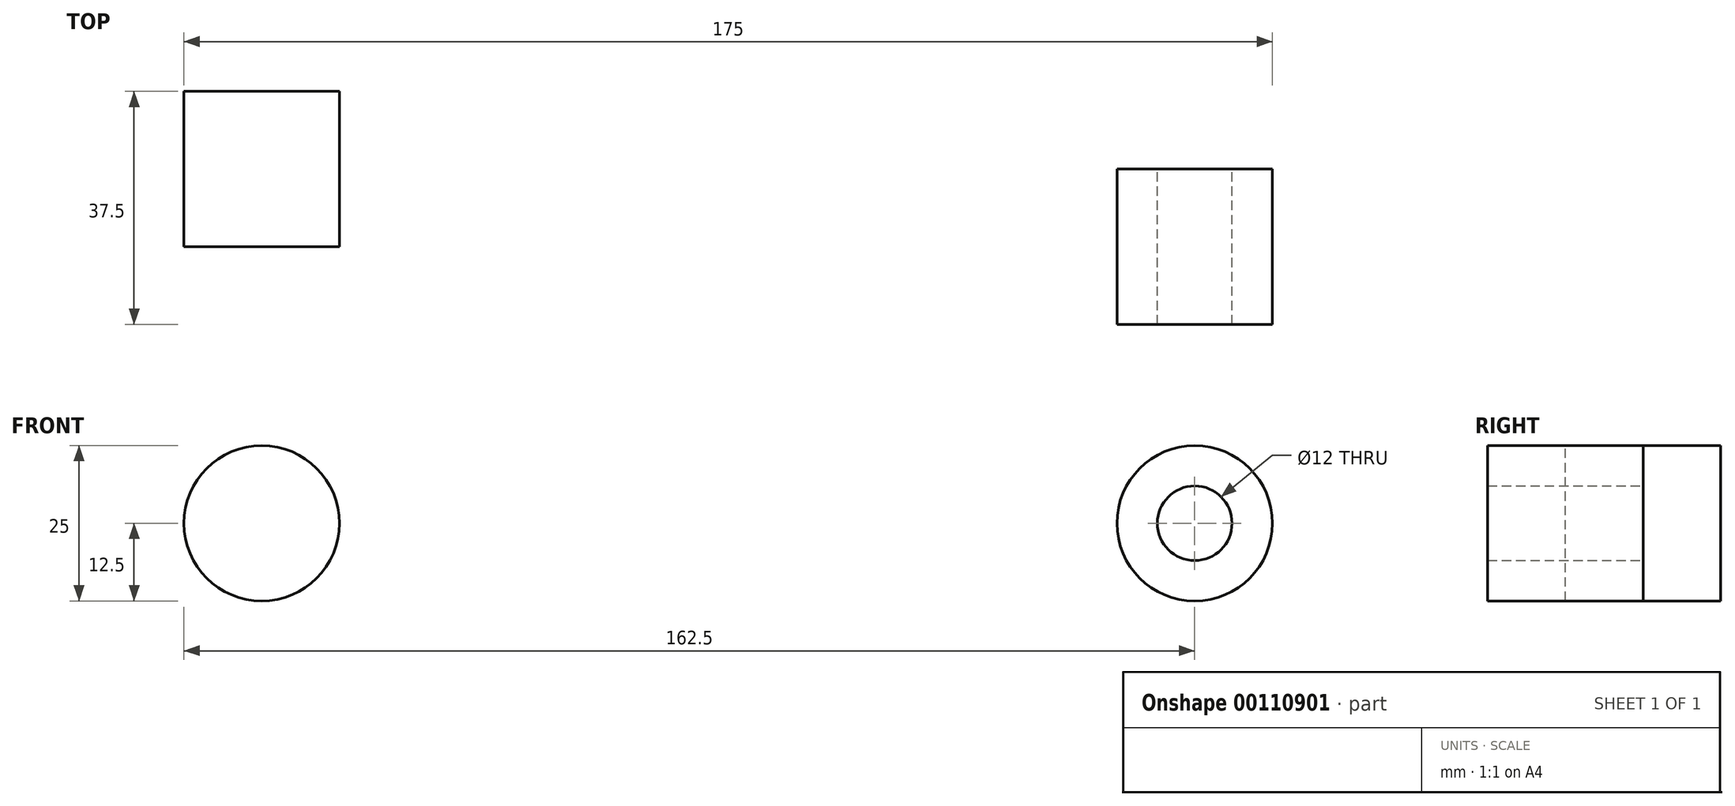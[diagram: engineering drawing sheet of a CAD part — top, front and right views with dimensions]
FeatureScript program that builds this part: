
annotation { "Feature Type Name" : "Feature", "Feature Type Description" : "" }
export const myFeature = defineFeature(function(context is Context, id is Id, definition is map)
    precondition{}
    {
        {
            var Q0;
            Q0=qCreatedBy(makeId("Top.planeOp"),FACE);
            var sketch = newSketch(context, id + "F0", { "sketchPlane" : qUnion([Q0])});
            skLineSegment(sketch, "E0.bottom", {"start": v(0, 25) * mm, "end": v(-25, 25) * mm});
            skLineSegment(sketch, "E0.top", {"start": v(0, 0) * mm, "end": v(-25, 0) * mm});
            skLineSegment(sketch, "E0.left", {"start": v(0, 25) * mm, "end": v(0, 0) * mm});
            skLineSegment(sketch, "E0.right", {"start": v(-25, 25) * mm, "end": v(-25, 0) * mm});
            skLineSegment(sketch, "E1", {"start": v(-12.5, 25) * mm, "end": v(-12.5, 0) * mm, "construction": true});
            skLineSegment(sketch, "E2", {"start": v(-61.4, 0) * mm, "end": v(112.5, 0) * mm, "construction": true});
            skLineSegment(sketch, "E3", {"start": v(112.5, 0) * mm, "end": v(150, 0) * mm});
            skLineSegment(sketch, "E4", {"start": v(150, 12.5) * mm, "end": v(150, -12.5) * mm});
            skLineSegment(sketch, "E5", {"start": v(125, -12.5) * mm, "end": v(150, -12.5) * mm});
            skLineSegment(sketch, "E6", {"start": v(125, -12.5) * mm, "end": v(125, 12.5) * mm});
            skLineSegment(sketch, "E7", {"start": v(150, 12.5) * mm, "end": v(125, 12.5) * mm});
            skLineSegment(sketch, "E8", {"start": v(137.5, 12.5) * mm, "end": v(137.5, -12.5) * mm, "construction": true});
            skLineSegment(sketch, "E9", {"start": v(125, 0) * mm, "end": v(150, 0) * mm, "construction": true});
            skLineSegment(sketch, "E10", {"start": v(-25, 12) * mm, "end": v(0, 12) * mm});
            skLineSegment(sketch, "E11", {"start": v(0, 12) * mm, "end": v(12.5, 12) * mm});
            skArc(sketch, "E12", {"start": v(48.5, 0) * mm, "mid": v(31.47, 8.92) * mm, "end": v(12.5, 12) * mm});
            skArc(sketch, "E13", {"start": v(48.5, 0) * mm, "mid": v(80.5, -10.67) * mm, "end": v(112.5, 0) * mm});
            skLineSegment(sketch, "E14", {"start": v(112.5, 0) * mm, "end": v(125, 0) * mm});
            skSolve(sketch);
        }
        {
            var Q0;
            Q0=qCreatedBy(makeId("Right.planeOp"),FACE);
            var sketch = newSketch(context, id + "F1", { "sketchPlane" : qUnion([Q0])});
            skCircle(sketch, "E15", {"center": v(12, 0) * mm, "radius": 7.5 * mm});
            skSolve(sketch);
        }
        {
            var Q0;
            Q0=qCreatedBy(makeId("Front.planeOp"),FACE);
            var sketch = newSketch(context, id + "F2", { "sketchPlane" : qUnion([Q0])});
            skCircle(sketch, "E16", {"center": v(-12.5, 0) * mm, "radius": 12.5 * mm});
            skCircle(sketch, "E17", {"center": v(-12.5, 0) * mm, "radius": 6 * mm});
            skCircle(sketch, "E18", {"center": v(137.5, 0) * mm, "radius": 12.5 * mm});
            skCircle(sketch, "E19", {"center": v(137.5, 0) * mm, "radius": 6 * mm});
            skSolve(sketch);
        }
        {
            var Q0;
            Q0=makeQuery(id+"F2.imprint","IMPRINT",FACE,{"disambiguationData":[TD([[makeQuery(id+"F2.imprint","IMPRINT",EDGE,{"derivedFrom":sQuery(id+"F2.wireOp",EDGE,"E16")}),1.0]])]});
            var Q1;
            Q1=makeQuery(id+"F2.imprint","IMPRINT",FACE,{"disambiguationData":[TD([[makeQuery(id+"F2.imprint","IMPRINT",EDGE,{"derivedFrom":sQuery(id+"F2.wireOp",EDGE,"E17")}),1.0]])]});
            extrude(context, id + "F3", {"entities" : qUnion([Q0, Q1]), "oppositeDirection" : true, "depth" : 25 * mm});
        }
        {
            var Q0;
            Q0=makeQuery(id+"F2.imprint","IMPRINT",FACE,{"disambiguationData":[TD([[makeQuery(id+"F2.imprint","IMPRINT",EDGE,{"derivedFrom":sQuery(id+"F2.wireOp",EDGE,"E18")}),1.0]])]});
            extrude(context, id + "F4", {"entities" : qUnion([Q0]), "endBound" : BoundingType.SYMMETRIC, "depth" : 25 * mm});
        }
    });
